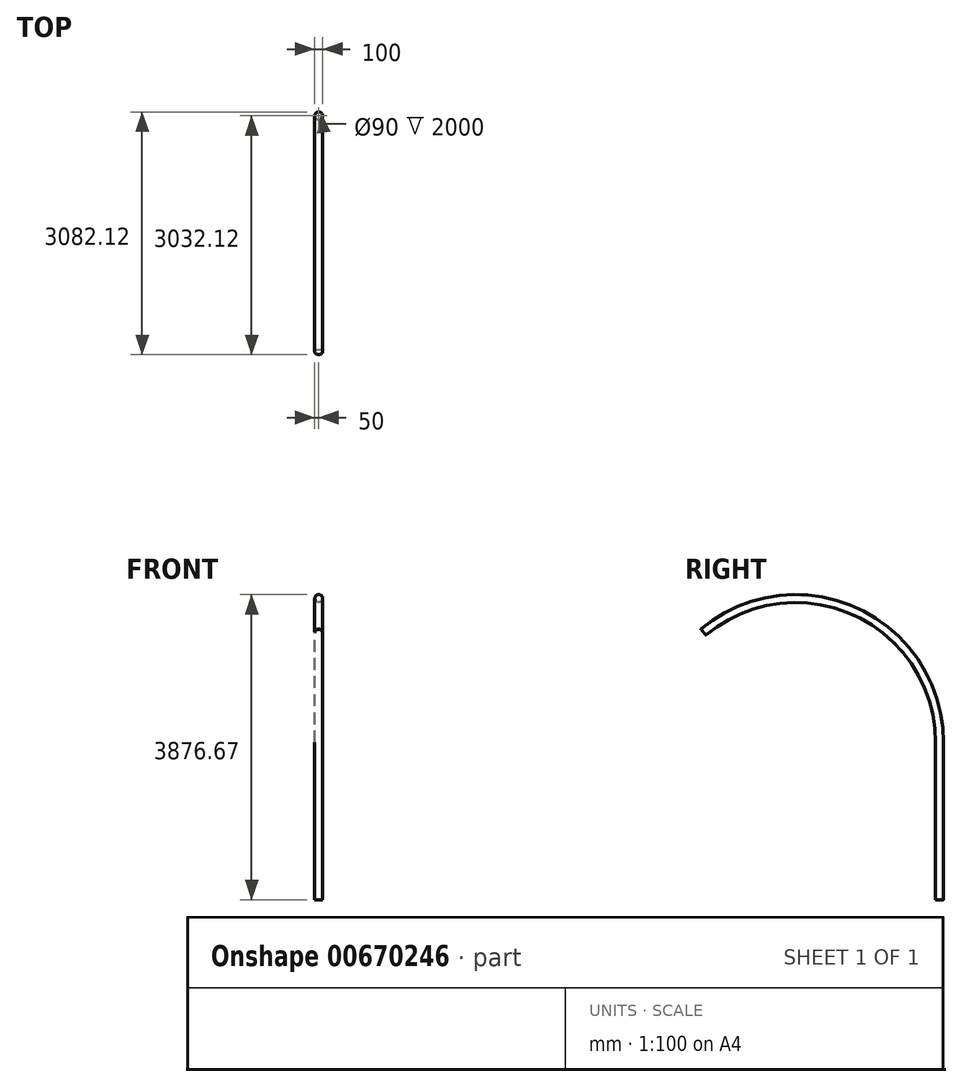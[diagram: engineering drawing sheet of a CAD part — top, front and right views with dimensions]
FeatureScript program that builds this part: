
annotation { "Feature Type Name" : "Feature", "Feature Type Description" : "" }
export const myFeature = defineFeature(function(context is Context, id is Id, definition is map)
    precondition{}
    {
        {
            var Q0;
            Q0=qCreatedBy(makeId("Right.planeOp"),FACE);
            var sketch = newSketch(context, id + "F0", { "sketchPlane" : qUnion([Q0])});
            skLineSegment(sketch, "E0", {"start": v(0, 0) * mm, "end": v(0, 2000) * mm});
            skPoint(sketch, "E1.end.orphan", {"position": v(-1213.18, 2000) * mm});
            skArc(sketch, "E2", {"start": v(0, 2000) * mm, "mid": v(-1054.2, 3655.3) * mm, "end": v(-3000, 3400) * mm});
            skLineSegment(sketch, "E3", {"start": v(0, 2000) * mm, "end": v(-3000, 3400) * mm, "construction": true});
            skPoint(sketch, "E4.orphan", {"position": v(-3652.72, 1952.55) * mm});
            skSolve(sketch);
        }
        {
            var Q0;
            Q0=qCreatedBy(makeId("Top.planeOp"),FACE);
            var sketch = newSketch(context, id + "F1", { "sketchPlane" : qUnion([Q0])});
            skCircle(sketch, "E5", {"center": v(0, 0) * mm, "radius": 50 * mm});
            skCircle(sketch, "E6", {"center": v(0, 0) * mm, "radius": 45 * mm});
            skSolve(sketch);
        }
        {
            var Q0;
            Q0=makeQuery(id+"F1.imprint","IMPRINT",FACE,{"disambiguationData":[TD([[makeQuery(id+"F1.imprint","IMPRINT",EDGE,{"derivedFrom":sQuery(id+"F1.wireOp",EDGE,"E5")}),1.0]])]});
            var Q1;
            Q1=sQuery(id+"F0.wireOp",EDGE,"E0");
            var Q2;
            Q2=sQuery(id+"F0.wireOp",EDGE,"E2");
            sweep(context, id + "F2", {"profiles" : qUnion([Q0]), "path" : qUnion([Q1, Q2])});
        }
    });
